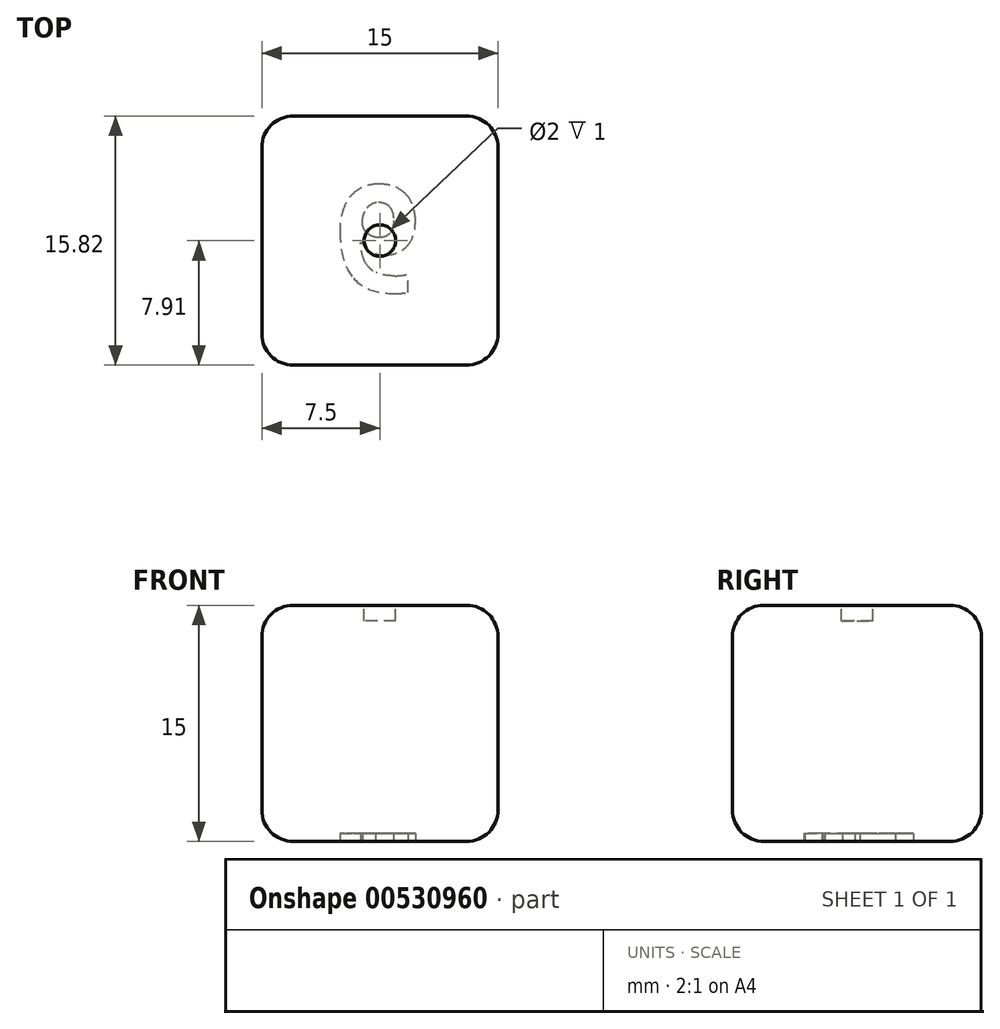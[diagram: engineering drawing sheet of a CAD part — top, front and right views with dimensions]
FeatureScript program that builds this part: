
annotation { "Feature Type Name" : "Feature", "Feature Type Description" : "" }
export const myFeature = defineFeature(function(context is Context, id is Id, definition is map)
    precondition{}
    {
        {
            var Q0;
            Q0=qCreatedBy(makeId("Top.planeOp"),FACE);
            var sketch = newSketch(context, id + "F0", { "sketchPlane" : qUnion([Q0])});
            skLineSegment(sketch, "E0.bottom", {"start": v(-7.5, 7.9) * mm, "end": v(7.5, 7.9) * mm});
            skLineSegment(sketch, "E0.top", {"start": v(-7.5, -7.9) * mm, "end": v(7.5, -7.9) * mm});
            skLineSegment(sketch, "E0.left", {"start": v(-7.5, 7.9) * mm, "end": v(-7.5, -7.9) * mm});
            skLineSegment(sketch, "E0.right", {"start": v(7.5, 7.9) * mm, "end": v(7.5, -7.9) * mm});
            skPoint(sketch, "E0.middle", {"position": v(0, 0) * mm});
            skSolve(sketch);
        }
        {
            var Q0;
            Q0 = qSketchRegion(id + "F0", true);
            extrude(context, id + "F1", {"entities" : qUnion([Q0]), "depth" : 15 * mm, "offsetDistance" : 25 * mm});
        }
        {
            var Q0;
            Q0=makeQuery(id+"F1.opExtrude","CAP_EDGE",EDGE,{"disambiguationData":[OSD([sQuery(id+"F0.wireOp",EDGE,"E0.top")])],"isStart":false});
            var Q1;
            Q1=makeQuery(id+"F1.opExtrude","CAP_EDGE",EDGE,{"disambiguationData":[OSD([sQuery(id+"F0.wireOp",EDGE,"E0.right")])],"isStart":false});
            var Q2;
            Q2=makeQuery(id+"F1.opExtrude","CAP_EDGE",EDGE,{"disambiguationData":[OSD([sQuery(id+"F0.wireOp",EDGE,"E0.bottom")])],"isStart":false});
            var Q3;
            Q3=makeQuery(id+"F1.opExtrude","CAP_EDGE",EDGE,{"disambiguationData":[OSD([sQuery(id+"F0.wireOp",EDGE,"E0.left")])],"isStart":false});
            var Q4;
            Q4=makeQuery(id+"F1.opExtrude","CAP_EDGE",EDGE,{"disambiguationData":[OSD([sQuery(id+"F0.wireOp",EDGE,"E0.top")])],"isStart":true});
            var Q5;
            Q5=makeQuery(id+"F1.opExtrude","CAP_EDGE",EDGE,{"disambiguationData":[OSD([sQuery(id+"F0.wireOp",EDGE,"E0.right")])],"isStart":true});
            var Q6;
            Q6=makeQuery(id+"F1.opExtrude","SWEPT_EDGE",EDGE,{"disambiguationData":[OSD([sQuery(id+"F0.wireOp",EDGE,"E0.top"),sQuery(id+"F0.wireOp",EDGE,"E0.left")])]});
            var Q7;
            Q7=makeQuery(id+"F1.opExtrude","SWEPT_EDGE",EDGE,{"disambiguationData":[OSD([sQuery(id+"F0.wireOp",EDGE,"E0.top"),sQuery(id+"F0.wireOp",EDGE,"E0.right")])]});
            var Q8;
            Q8=makeQuery(id+"F1.opExtrude","SWEPT_EDGE",EDGE,{"disambiguationData":[OSD([sQuery(id+"F0.wireOp",EDGE,"E0.bottom"),sQuery(id+"F0.wireOp",EDGE,"E0.right")])]});
            var Q9;
            Q9=makeQuery(id+"F1.opExtrude","SWEPT_EDGE",EDGE,{"disambiguationData":[OSD([sQuery(id+"F0.wireOp",EDGE,"E0.bottom"),sQuery(id+"F0.wireOp",EDGE,"E0.left")])]});
            var Q10;
            Q10=makeQuery(id+"F1.opExtrude","CAP_EDGE",EDGE,{"disambiguationData":[OSD([sQuery(id+"F0.wireOp",EDGE,"E0.left")])],"isStart":true});
            var Q11;
            Q11=makeQuery(id+"F1.opExtrude","CAP_EDGE",EDGE,{"disambiguationData":[OSD([sQuery(id+"F0.wireOp",EDGE,"E0.bottom")])],"isStart":true});
            fillet(context, id + "F2", {"entities" : qUnion([Q0, Q1, Q2, Q3, Q4, Q5, Q6, Q7, Q8, Q9, Q10, Q11]), "radius" : 2 * mm, "tangentPropagation" : true, "allowEdgeOverflow" : false});
        }
        {
            var Q0;
            Q0=makeQuery(id+"F1.opExtrude","CAP_FACE",FACE,{"disambiguationData":[OSD([sQuery(id+"F0.wireOp",EDGE,"E0.bottom"),sQuery(id+"F0.wireOp",EDGE,"E0.top"),sQuery(id+"F0.wireOp",EDGE,"E0.left"),sQuery(id+"F0.wireOp",EDGE,"E0.right")])],"isStart":false});
            var sketch = newSketch(context, id + "F3", { "sketchPlane" : qUnion([Q0])});
            skCircle(sketch, "E1", {"center": v(0, 0) * mm, "radius": 1 * mm});
            skSolve(sketch);
        }
        {
            var Q0;
            Q0 = qSketchRegion(id + "F3", true);
            extrude(context, id + "F4", {"entities" : qUnion([Q0]), "operationType" : NewBodyOperationType.REMOVE, "oppositeDirection" : true, "depth" : 1 * mm, "offsetDistance" : 25 * mm});
        }
        {
            var Q0;
            Q0=makeQuery(id+"F1.opExtrude","CAP_FACE",FACE,{"disambiguationData":[OSD([sQuery(id+"F0.wireOp",EDGE,"E0.bottom"),sQuery(id+"F0.wireOp",EDGE,"E0.top"),sQuery(id+"F0.wireOp",EDGE,"E0.left"),sQuery(id+"F0.wireOp",EDGE,"E0.right")])],"isStart":true});
            var sketch = newSketch(context, id + "F5", { "sketchPlane" : qUnion([Q0])});
            skText(sketch, "E2", { "text": "6", "fontName": "OpenSans-Bold.ttf"});
            const initialGuessF5  = {"E2": [-0.00287, -0.0035, 1, 0, 0.00684]};
            skSetInitialGuess(sketch, initialGuessF5);
            skSolve(sketch);
        }
        {
            var Q0;
            Q0 = qSketchRegion(id + "F5", true);
            extrude(context, id + "F6", {"entities" : qUnion([Q0]), "operationType" : NewBodyOperationType.REMOVE, "oppositeDirection" : true, "depth" : 0.5 * mm, "offsetDistance" : 25 * mm});
        }
    });
